# Revit family: okamura_L143HRN_Lives Work Lounge Chair_Without Arm, High Back, Black Aluminium Base, Black Body
name_source: partatom
category: Furniture
revit_build: Autodesk Revit 2016 (Build: 20150714_1515(x64)
units: mm (PartAtom-declared; Revit-internal decimal feet)

## family parameters
Always vertical = Yes
Cut with Voids When Loaded = No
OmniClass Number = 23.40.20.00
OmniClass Title = General Furniture and Specialties
Room Calculation Point = No
Shared = No
Work Plane-Based = No

## types (22) — shared parameters
Assembly Code = E2020200
Body & Base = okm_Z25
D = 690 mm  [stored 2.26378 ft]
H = 945 mm  [stored 3.10039 ft]
Keynote = 12490
Kind = Chair
Manufacturer = Okamura Corporation
Product Categories = Seating
URL = http://www.okamura.co.jp
W = 590 mm  [stored 1.9357 ft]

## per-type parameters (varying)
| type | Color | Product Code/Color |
| FXW2(Beige) | okm_FXW2 | L143HRN_FXW2 |
| FXW3(Dark Brown) | okm_FXW3 | L143HRN_FXW3 |
| FXW1(Gray) | okm_FXW1 | L143HRN_FXW1 |
| FXW4(Indigo) | okm_FXW4 | L143HRN_FXW4 |
| FXW9(Sage) | okm_FXW9 | L143HRN_FXW9 |
| FXW5(Dark Green) | okm_FXW5 | L143HRN_FXW5 |
| FXW7(Yellow) | okm_FXW7 | L143HRN_FXW7 |
| FXW6(Terracotta) | okm_FXW6 | L143HRN_FXW6 |
| FXW8(Pale Pink) | okm_FXW8 | L143HRN_FXW8 |
| P676(Black) | okm_P676 | L143HRN_P676 |
| PC18(White) | okm_PC18 | L143HRN_PC18 |
| PD98(Camel) | okm_PD98 | L143HRN_PD98 |
| FKY1(Dark Gray) | okm_FKY1 | L143HRN_FKY1 |
| FKY2(Gray) | okm_FKY2 | L143HRN_FKY2 |
| FKY3(Light Gray) | okm_FKY3 | L143HRN_FKY3 |
| FKY4(Dark Blue) | okm_FKY4 | L143HRN_FKY4 |
| FKY5(Dark Green) | okm_FKY5 | L143HRN_FKY5 |
| FKY6(Sage) | okm_FKY6 | L143HRN_FKY6 |
| FKY7(Beige) | okm_FKY7 | L143HRN_FKY7 |
| FKY8(Terracotta) | okm_FKY8 | L143HRN_FKY8 |
| FKY9(Yellow Green) | okm_FKY9 | L143HRN_FKY9 |
| FKZ7(Pale Pink) | okm_FKZ7 | L143HRN_FKZ7 |

note: [stored X ft] marks values corroborated as IEEE doubles in the binary element streams (Revit-internal decimal feet)
